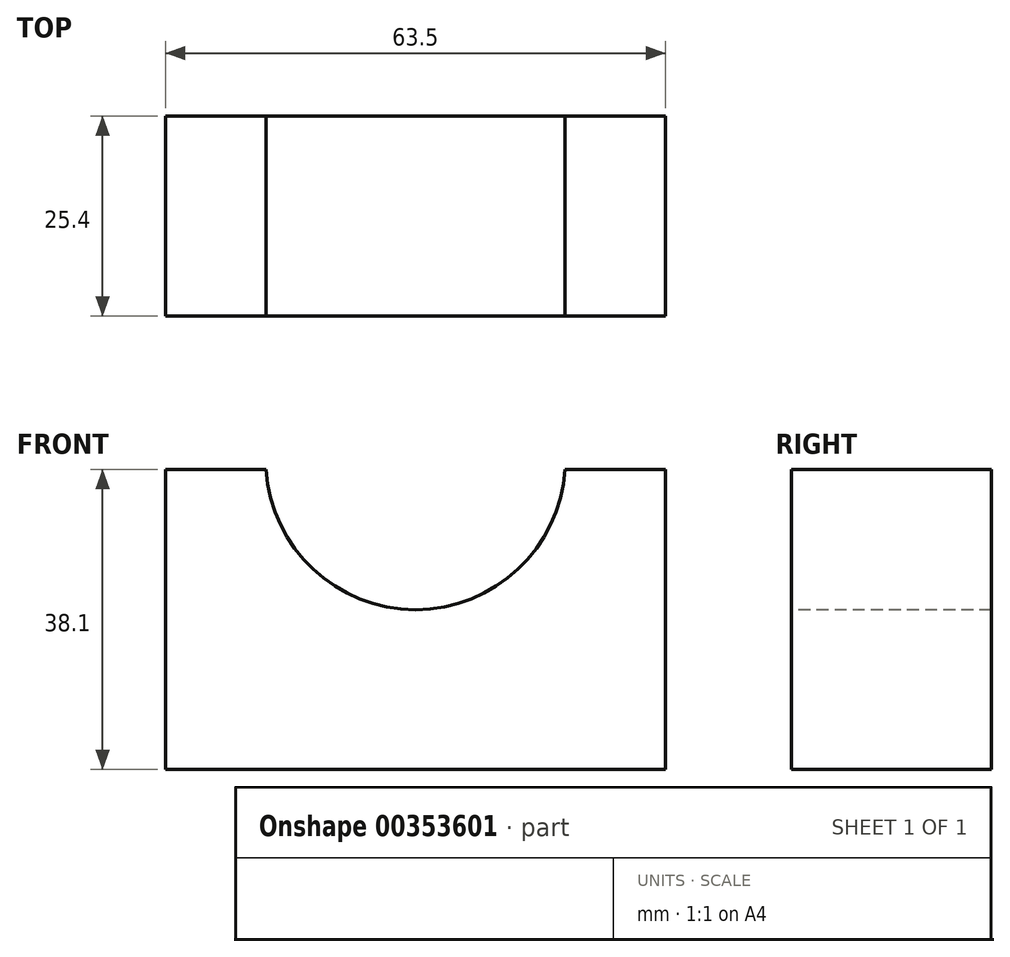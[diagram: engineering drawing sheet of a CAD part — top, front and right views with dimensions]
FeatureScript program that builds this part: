
annotation { "Feature Type Name" : "Feature", "Feature Type Description" : "" }
export const myFeature = defineFeature(function(context is Context, id is Id, definition is map)
    precondition{}
    {
        {
            var Q0;
            Q0=qCreatedBy(makeId("Front.planeOp"),FACE);
            var sketch = newSketch(context, id + "F0", { "sketchPlane" : qUnion([Q0])});
            skLineSegment(sketch, "E0.bottom", {"start": v(0, 0) * mm, "end": v(63.5, 0) * mm});
            skLineSegment(sketch, "E0.top", {"start": v(0, 38.1) * mm, "end": v(63.5, 38.1) * mm});
            skLineSegment(sketch, "E0.left", {"start": v(0, 0) * mm, "end": v(0, 38.1) * mm});
            skLineSegment(sketch, "E0.right", {"start": v(63.5, 0) * mm, "end": v(63.5, 38.1) * mm});
            skSolve(sketch);
        }
        {
            var Q0;
            Q0=makeQuery(id+"F0.imprint","IMPRINT",FACE,{"disambiguationData":[TD([[makeQuery(id+"F0.imprint","IMPRINT",EDGE,{"derivedFrom":sQuery(id+"F0.wireOp",EDGE,"E0.bottom")}),1.0]])]});
            extrude(context, id + "F1", {"entities" : qUnion([Q0]), "depth" : 25.4 * mm});
        }
        {
            var Q0;
            Q0=makeQuery(id+"F1.opExtrude","CAP_FACE",FACE,{"disambiguationData":[OSD([sQuery(id+"F0.wireOp",EDGE,"E0.bottom"),sQuery(id+"F0.wireOp",EDGE,"E0.top"),sQuery(id+"F0.wireOp",EDGE,"E0.left"),sQuery(id+"F0.wireOp",EDGE,"E0.right")])],"isStart":false});
            var sketch = newSketch(context, id + "F2", { "sketchPlane" : qUnion([Q0])});
            skArc(sketch, "E1", {"start": v(12.74, 38.1) * mm, "mid": v(31.75, 20.3) * mm, "end": v(50.76, 38.1) * mm});
            skLineSegment(sketch, "E2", {"start": v(12.74, 38.1) * mm, "end": v(50.76, 38.1) * mm});
            skSolve(sketch);
        }
        {
            var Q0;
            Q0=makeQuery(id+"F2.imprint","IMPRINT",FACE,{"disambiguationData":[TD([[makeQuery(id+"F2.imprint","IMPRINT",EDGE,{"derivedFrom":sQuery(id+"F2.wireOp",EDGE,"E1")}),1.0]])]});
            extrude(context, id + "F3", {"entities" : qUnion([Q0]), "operationType" : NewBodyOperationType.REMOVE, "oppositeDirection" : true, "depth" : 25.4 * mm});
        }
    });
